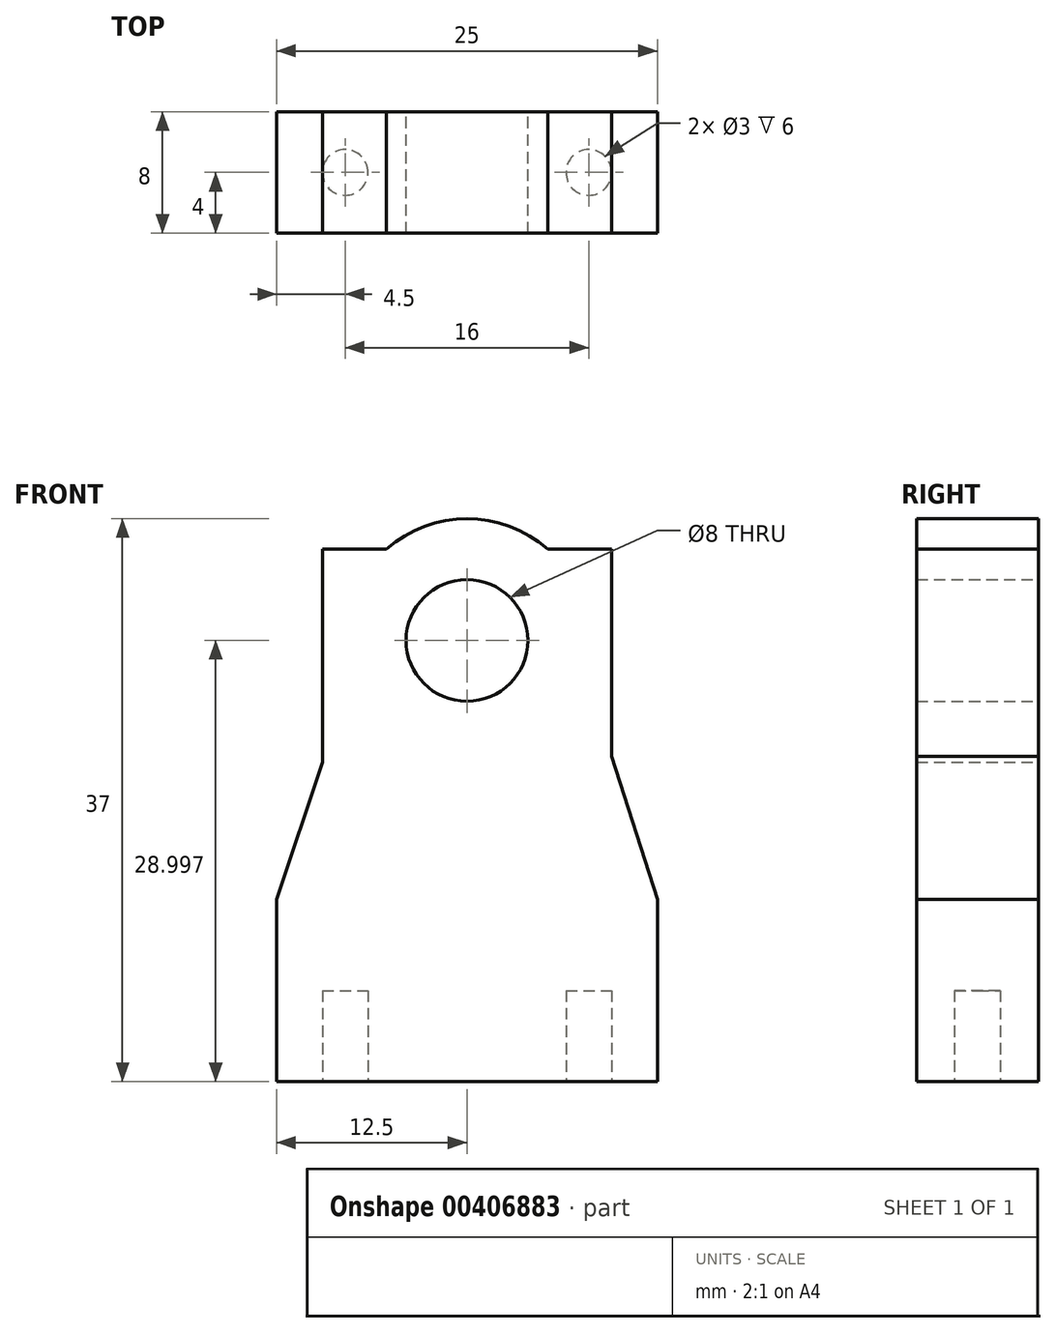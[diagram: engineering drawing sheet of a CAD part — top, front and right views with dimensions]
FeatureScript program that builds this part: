
annotation { "Feature Type Name" : "Feature", "Feature Type Description" : "" }
export const myFeature = defineFeature(function(context is Context, id is Id, definition is map)
    precondition{}
    {
        {
            var Q0;
            Q0=qCreatedBy(makeId("Front.planeOp"),FACE);
            var sketch = newSketch(context, id + "F0", { "sketchPlane" : qUnion([Q0])});
            skLineSegment(sketch, "E0", {"start": v(-12.5, -15.46) * mm, "end": v(12.5, -15.46) * mm});
            skLineSegment(sketch, "E1", {"start": v(-12.5, -15.46) * mm, "end": v(-12.5, -3.46) * mm});
            skLineSegment(sketch, "E2", {"start": v(12.5, -15.46) * mm, "end": v(12.5, -3.46) * mm});
            skPoint(sketch, "E3", {"position": v(0, 13.54) * mm});
            skLineSegment(sketch, "E4", {"start": v(9.5, 19.54) * mm, "end": v(9.5, 5.93) * mm});
            skLineSegment(sketch, "E5", {"start": v(-9.5, 19.54) * mm, "end": v(-9.5, 5.54) * mm});
            skLineSegment(sketch, "E6", {"start": v(9.5, 19.54) * mm, "end": v(5.3, 19.54) * mm});
            skLineSegment(sketch, "E7", {"start": v(-9.5, 19.54) * mm, "end": v(-5.3, 19.54) * mm});
            skLineSegment(sketch, "E8", {"start": v(-12.5, -3.46) * mm, "end": v(-9.5, 5.54) * mm});
            skLineSegment(sketch, "E9", {"start": v(9.5, 5.93) * mm, "end": v(12.5, -3.46) * mm});
            skArc(sketch, "E10", {"start": v(5.3, 19.54) * mm, "mid": v(0, 21.54) * mm, "end": v(-5.3, 19.54) * mm});
            skCircle(sketch, "E11", {"center": v(0, 13.54) * mm, "radius": 4 * mm});
            skSolve(sketch);
        }
        {
            var Q0;
            Q0=makeQuery(id+"F0.imprint","IMPRINT",FACE,{"disambiguationData":[TD([[makeQuery(id+"F0.imprint","IMPRINT",EDGE,{"derivedFrom":sQuery(id+"F0.wireOp",EDGE,"E0")}),1.0]])]});
            extrude(context, id + "F1", {"entities" : qUnion([Q0]), "endBound" : BoundingType.SYMMETRIC, "depth" : 8 * mm});
        }
        {
            var Q0;
            Q0=makeQuery(id+"F1.opExtrude","SWEPT_FACE",FACE,{"disambiguationData":[OSD([sQuery(id+"F0.wireOp",EDGE,"E0")])]});
            var sketch = newSketch(context, id + "F2", { "sketchPlane" : qUnion([Q0])});
            skCircle(sketch, "E12", {"center": v(-8, 0) * mm, "radius": 1.5 * mm});
            skCircle(sketch, "E13", {"center": v(8, 0) * mm, "radius": 1.5 * mm});
            skSolve(sketch);
        }
        {
            var Q0;
            Q0=makeQuery(id+"F2.imprint","IMPRINT",FACE,{"disambiguationData":[TD([[makeQuery(id+"F2.imprint","IMPRINT",EDGE,{"derivedFrom":sQuery(id+"F2.wireOp",EDGE,"E12")}),1.0]])]});
            var Q1;
            Q1=makeQuery(id+"F2.imprint","IMPRINT",FACE,{"disambiguationData":[TD([[makeQuery(id+"F2.imprint","IMPRINT",EDGE,{"derivedFrom":sQuery(id+"F2.wireOp",EDGE,"E13")}),1.0]])]});
            extrude(context, id + "F3", {"entities" : qUnion([Q0, Q1]), "operationType" : NewBodyOperationType.REMOVE, "oppositeDirection" : true, "depth" : 6 * mm});
        }
    });
